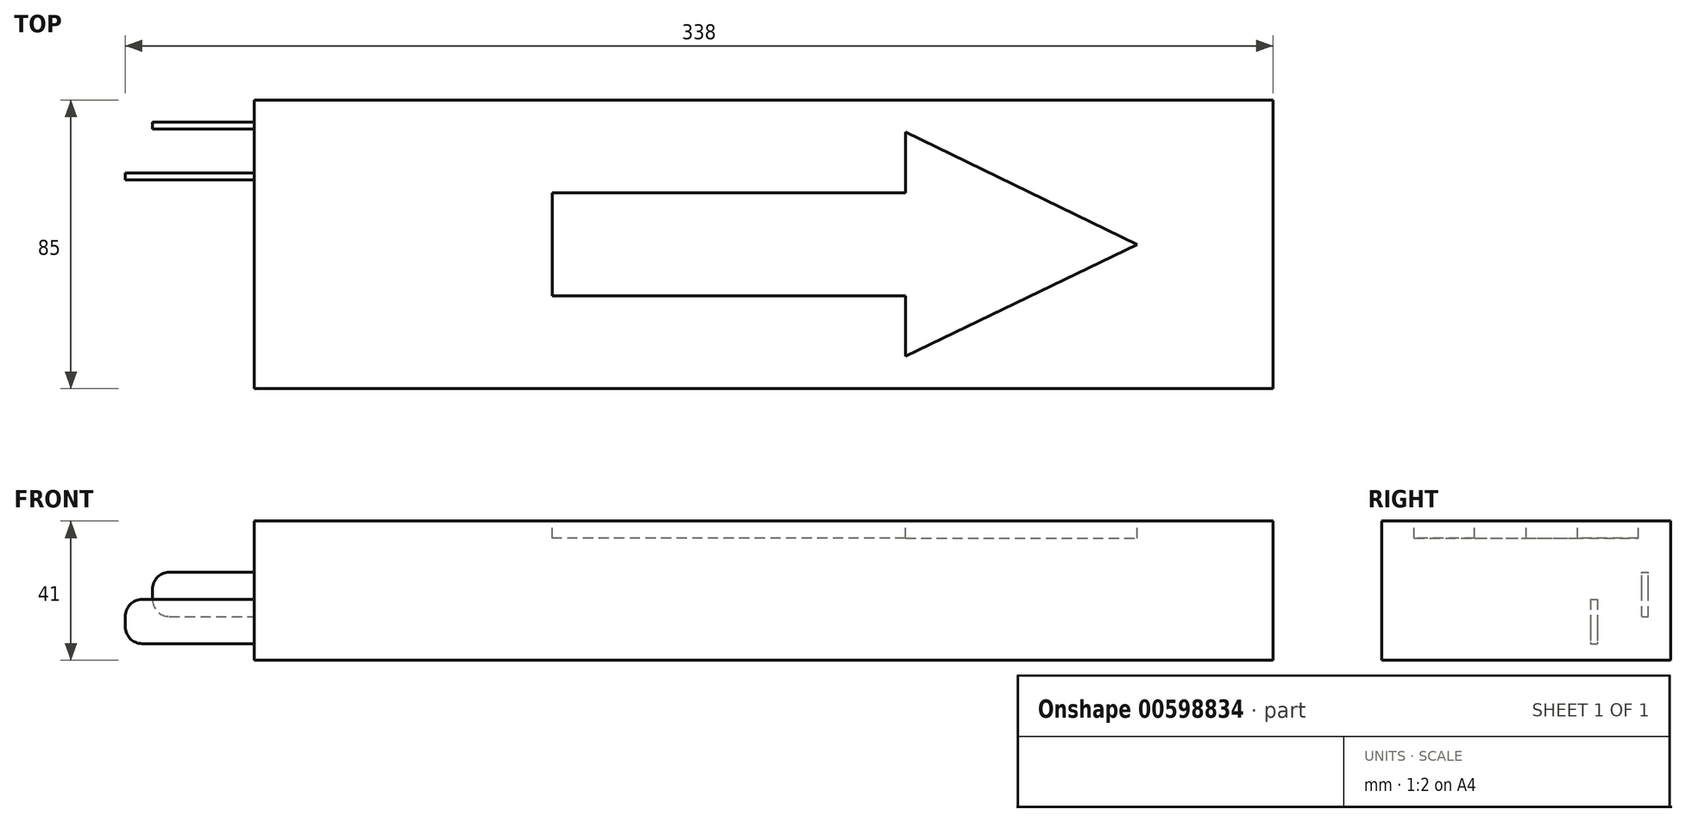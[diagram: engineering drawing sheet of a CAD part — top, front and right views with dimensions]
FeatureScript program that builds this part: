
annotation { "Feature Type Name" : "Feature", "Feature Type Description" : "" }
export const myFeature = defineFeature(function(context is Context, id is Id, definition is map)
    precondition{}
    {
        {
            var Q0;
            Q0=qCreatedBy(makeId("Top.planeOp"),FACE);
            var sketch = newSketch(context, id + "F0", { "sketchPlane" : qUnion([Q0])});
            skLineSegment(sketch, "E0.bottom", {"start": v(150, -42.5) * mm, "end": v(-150, -42.5) * mm});
            skLineSegment(sketch, "E0.top", {"start": v(150, 42.5) * mm, "end": v(-150, 42.5) * mm});
            skLineSegment(sketch, "E0.left", {"start": v(150, -42.5) * mm, "end": v(150, 42.5) * mm});
            skLineSegment(sketch, "E0.right", {"start": v(-150, -42.5) * mm, "end": v(-150, 42.5) * mm});
            skPoint(sketch, "E0.middle", {"position": v(0, 0) * mm});
            skSolve(sketch);
        }
        {
            var Q0;
            Q0=makeQuery(id+"F0.imprint","IMPRINT",FACE,{"disambiguationData":[TD([[makeQuery(id+"F0.imprint","IMPRINT",EDGE,{"derivedFrom":sQuery(id+"F0.wireOp",EDGE,"E0.bottom")}),-1.0]])]});
            extrude(context, id + "F1", {"entities" : qUnion([Q0]), "depth" : 41 * mm, "offsetDistance" : 25 * mm});
        }
        {
            var Q0;
            Q0=makeQuery(id+"F1.opExtrude","SWEPT_FACE",FACE,{"disambiguationData":[OSD([sQuery(id+"F0.wireOp",EDGE,"E0.right")])]});
            var sketch = newSketch(context, id + "F2", { "sketchPlane" : qUnion([Q0])});
            skLineSegment(sketch, "E1.bottom", {"start": v(-34, 12.9) * mm, "end": v(-36, 12.9) * mm});
            skLineSegment(sketch, "E1.top", {"start": v(-34, 25.9) * mm, "end": v(-36, 25.9) * mm});
            skLineSegment(sketch, "E1.left", {"start": v(-34, 12.9) * mm, "end": v(-34, 25.9) * mm});
            skLineSegment(sketch, "E1.right", {"start": v(-36, 12.9) * mm, "end": v(-36, 25.9) * mm});
            skPoint(sketch, "E1.middle", {"position": v(-35, 19.4) * mm});
            skSolve(sketch);
        }
        {
            var Q0;
            Q0=makeQuery(id+"F2.imprint","IMPRINT",FACE,{"disambiguationData":[TD([[makeQuery(id+"F2.imprint","IMPRINT",EDGE,{"derivedFrom":sQuery(id+"F2.wireOp",EDGE,"E1.bottom")}),1.0]])]});
            var sketch = newSketch(context, id + "F3", { "sketchPlane" : qUnion([Q0])});
            skLineSegment(sketch, "E2.bottom", {"start": v(-19, 17.9) * mm, "end": v(-21, 17.9) * mm});
            skLineSegment(sketch, "E2.top", {"start": v(-19, 4.9) * mm, "end": v(-21, 4.9) * mm});
            skLineSegment(sketch, "E2.left", {"start": v(-19, 17.9) * mm, "end": v(-19, 4.9) * mm});
            skLineSegment(sketch, "E2.right", {"start": v(-21, 17.9) * mm, "end": v(-21, 4.9) * mm});
            skPoint(sketch, "E2.middle", {"position": v(-20, 11.4) * mm});
            skSolve(sketch);
        }
        {
            var Q0;
            Q0 = qSketchRegion(id + "F3", true);
            extrude(context, id + "F4", {"entities" : qUnion([Q0]), "operationType" : NewBodyOperationType.ADD, "depth" : 38 * mm, "offsetDistance" : 25 * mm});
        }
        {
            var Q0;
            Q0 = qSketchRegion(id + "F2", true);
            extrude(context, id + "F5", {"entities" : qUnion([Q0]), "operationType" : NewBodyOperationType.ADD, "depth" : 30 * mm, "offsetDistance" : 25 * mm});
        }
        {
            var Q0;
            Q0=makeQuery(id+"F5.opExtrude","CAP_EDGE",EDGE,{"disambiguationData":[OSD([sQuery(id+"F2.wireOp",EDGE,"E1.top")])],"isStart":false});
            var Q1;
            Q1=makeQuery(id+"F5.opExtrude","CAP_EDGE",EDGE,{"disambiguationData":[OSD([sQuery(id+"F2.wireOp",EDGE,"E1.bottom")])],"isStart":false});
            fillet(context, id + "F6", {"entities" : qUnion([Q0, Q1]), "radius" : 5 * mm, "tangentPropagation" : true, "allowEdgeOverflow" : false});
        }
        {
            var Q0;
            Q0=makeQuery(id+"F4.opExtrude","CAP_EDGE",EDGE,{"disambiguationData":[OSD([sQuery(id+"F3.wireOp",EDGE,"E2.bottom")])],"isStart":false});
            var Q1;
            Q1=makeQuery(id+"F4.opExtrude","CAP_EDGE",EDGE,{"disambiguationData":[OSD([sQuery(id+"F3.wireOp",EDGE,"E2.top")])],"isStart":false});
            fillet(context, id + "F7", {"entities" : qUnion([Q0, Q1]), "radius" : 5 * mm, "tangentPropagation" : true, "allowEdgeOverflow" : false});
        }
        {
            var Q0;
            Q0=makeQuery(id+"F1.opExtrude","CAP_FACE",FACE,{"disambiguationData":[OSD([sQuery(id+"F0.wireOp",EDGE,"E0.bottom"),sQuery(id+"F0.wireOp",EDGE,"E0.top"),sQuery(id+"F0.wireOp",EDGE,"E0.left"),sQuery(id+"F0.wireOp",EDGE,"E0.right")])],"isStart":false});
            var sketch = newSketch(context, id + "F8", { "sketchPlane" : qUnion([Q0])});
            skLineSegment(sketch, "E3.bottom", {"start": v(41.77, -15.17) * mm, "end": v(-62.22, -15.17) * mm});
            skLineSegment(sketch, "E3.top", {"start": v(41.77, 15.17) * mm, "end": v(-62.22, 15.17) * mm});
            skLineSegment(sketch, "E3.right", {"start": v(-62.22, -15.17) * mm, "end": v(-62.22, 15.17) * mm});
            skPoint(sketch, "E3.middle", {"position": v(-10.22, 0) * mm});
            skLineSegment(sketch, "E4", {"start": v(109.96, 0) * mm, "end": v(41.77, 33.1) * mm});
            skPoint(sketch, "E4.startSnap0", {"position": v(41.77, 0) * mm});
            skPoint(sketch, "E4.endSnap0", {"position": v(41.77, 0) * mm});
            skLineSegment(sketch, "E5", {"start": v(41.77, 33.1) * mm, "end": v(41.77, 15.17) * mm});
            skLineSegment(sketch, "E6", {"start": v(41.77, -32.97) * mm, "end": v(109.96, 0) * mm});
            skLineSegment(sketch, "E7.trimOffspring", {"start": v(41.77, -15.17) * mm, "end": v(41.77, -32.97) * mm});
            skSolve(sketch);
        }
        {
            var Q0;
            Q0 = qSketchRegion(id + "F8", true);
            extrude(context, id + "F9", {"entities" : qUnion([Q0]), "operationType" : NewBodyOperationType.REMOVE, "oppositeDirection" : true, "depth" : 5 * mm, "offsetDistance" : 25 * mm});
        }
    });
